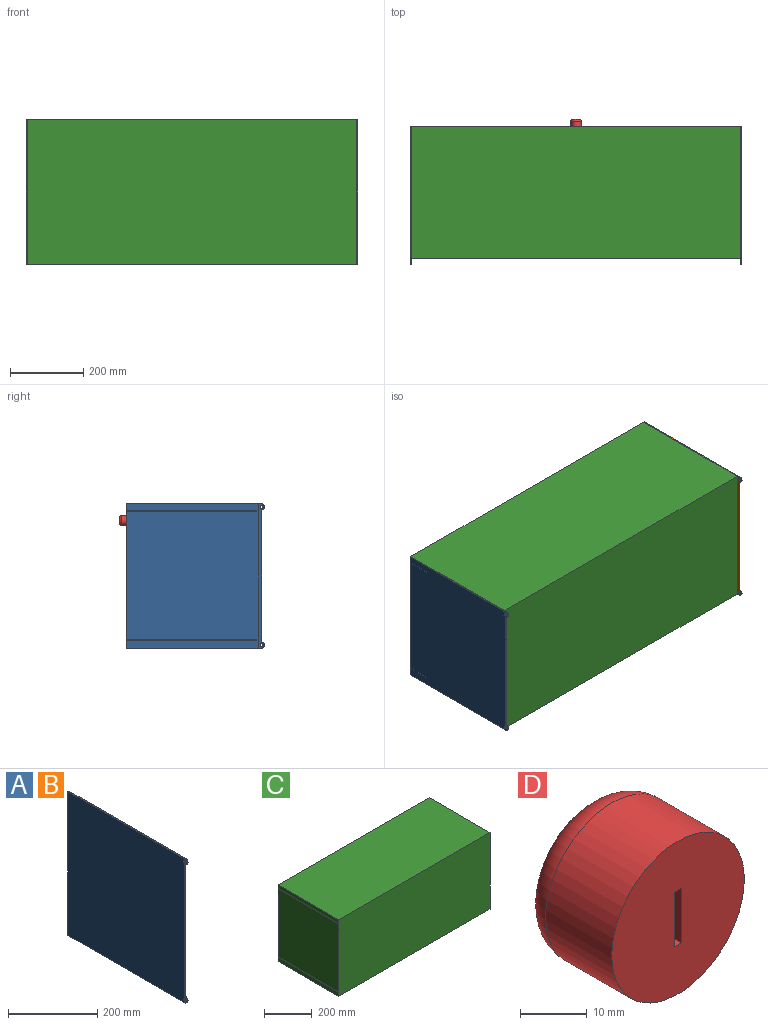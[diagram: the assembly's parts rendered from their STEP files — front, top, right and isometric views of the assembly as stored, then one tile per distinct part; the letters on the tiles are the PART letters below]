
ASSEMBLY  parts=4 mates=3
PART A: 10 faces, bbox 3.2x377.4x394.5 mm
  f0: cylinder r=7.87mm len=15.75mm, axis (-1,0,0), area 78.5mm2, adj f1,f7,f8,f9
  f1: plane 362.99x3.18mm, normal (0,-1,0), area 1152.5mm2, adj f0,f2,f8,f9
  f2: cylinder r=7.87mm len=15.75mm, axis (-1,0,0), area 78.5mm2, adj f1,f3,f8,f9
  f3: plane 369.49x3.18mm, normal (0,0,-1), area 1173.1mm2, adj f2,f4,f8,f9
  f4: plane 394.49x3.18mm, normal (0,1,0), area 1252.5mm2, adj f3,f7,f8,f9
  f5: cylinder r=4mm len=8mm, axis (-1,0,0), area 79.8mm2, adj f8,f9
  f6: cylinder r=4mm len=8mm, axis (-1,0,0), area 79.8mm2, adj f8,f9
  f7: plane 369.49x3.18mm, normal (0,0,1), area 1173.1mm2, adj f0,f4,f8,f9
  f8: plane 394.49x377.37mm, normal (1,0,0), area 145854.9mm2, adj f0,f1,f2,f3,f4,f5,f6,f7
  f9: plane 394.49x377.37mm, normal (-1,0,0), area 145854.9mm2, adj f0,f1,f2,f3,f4,f5,f6,f7
PART B: same geometry as A
PART C: 19 faces, bbox 900.1x362x394.5 mm
  f0: plane 900.11x355.6mm, normal (0,0,1), area 40917.3mm2, adj f1,f4,f8,f13,f14,f15,f16,f17
  f1: plane 900.11x350.19mm, normal (0,1,0), area 315208.6mm2, adj f0,f4,f8,f9
  f2: plane 900.11x17.95mm, normal (0,1,0), area 16159.6mm2, adj f4,f6,f8,f12
  f3: plane 900.11x20mm, normal (0,1,0), area 17999.1mm2, adj f4,f7,f8,f10
  f4: plane 394.49x361.95mm, normal (-1,0,0), area 140526.7mm2, adj f0,f1,f2,f3,f5,f6,f7,f9
  f5: plane 900.11x394.49mm, normal (0,-1,0), area 355083mm2, adj f4,f6,f7,f8
  f6: plane 900.11x361.95mm, normal (0,0,1), area 325795.7mm2, adj f2,f4,f5,f8
  f7: plane 900.11x361.95mm, normal (0,0,-1), area 325795.7mm2, adj f3,f4,f5,f8
  f8: plane 394.49x361.95mm, normal (1,0,0), area 140526.7mm2, adj f0,f1,f2,f3,f5,f6,f7,f9
  f9: plane 900.11x355.6mm, normal (0,0,-1), area 320080mm2, adj f1,f4,f8,f11
  f10: plane 900.11x355.6mm, normal (0,0,1), area 320080mm2, adj f3,f4,f8,f11
  f11: plane 900.11x3.18mm, normal (0,1,0), area 2857.9mm2, adj f4,f8,f9,f10
  f12: plane 900.11x355.6mm, normal (0,0,-1), area 320080mm2, adj f2,f4,f8,f13
  f13: plane 900.11x3.18mm, normal (0,1,0), area 2857.9mm2, adj f0,f4,f8,f12
  f14: plane 862.01x331.14mm, normal (0,-1,0), area 285445.1mm2, adj f0,f15,f17,f18
  f15: plane 331.14x323.85mm, normal (1,0,0), area 107239.1mm2, adj f0,f14,f16,f18
  f16: plane 862.01x331.14mm, normal (0,1,0), area 285445.1mm2, adj f0,f15,f17,f18
  f17: plane 331.14x323.85mm, normal (-1,0,0), area 107239.1mm2, adj f0,f14,f16,f18
  f18: plane 862.01x323.85mm, normal (0,0,1), area 279162.7mm2, adj f14,f15,f16,f17
PART D: 8 faces, bbox 30.3x19.1x30.3 mm
  f0: plane 19.05x1.5mm, normal (0,0,1), area 28.6mm2, adj f1,f3,f5,f6
  f1: plane 19.05x10mm, normal (-1,0,0), area 190.5mm2, adj f0,f2,f5,f6
  f2: plane 19.05x1.5mm, normal (0,0,-1), area 28.6mm2, adj f1,f3,f5,f6
  f3: plane 19.05x10mm, normal (1,0,0), area 190.5mm2, adj f0,f2,f5,f6
  f4: cylinder r=14mm len=28mm, axis (0,-1,0), area 1228.9mm2, adj f6,f7
  f5: plane 17.84x17.84mm, normal (0,1,0), area 235mm2, adj f0,f1,f2,f3,f7
  f6: plane 28x28mm, normal (0,-1,0), area 600.8mm2, adj f0,f1,f2,f3,f4
  f7: torus R=8.92mm, axis (0,1,0), area 609.4mm2, adj f4,f5
PLACE A t=(-474.11,6684.93,-2894.31)mm
PLACE B t=(429.17,6684.93,-2894.31)mm
PLACE C t=(-641.31,6684.93,-3899.62)mm
PLACE D t=(-641.24,6684.93,-3898.07)mm
MATE fastened A.f8 <-> C.f4  axis (1,0,0) through (-470.94,-1480.56,36.7)mm
MATE fastened C.f1 <-> D.f6  axis (0,1,0) through (-20.88,-1480.56,15.57)mm
MATE fastened B.f9 <-> C.f8  axis (-1,0,0) through (429.17,-1480.56,36.7)mm
